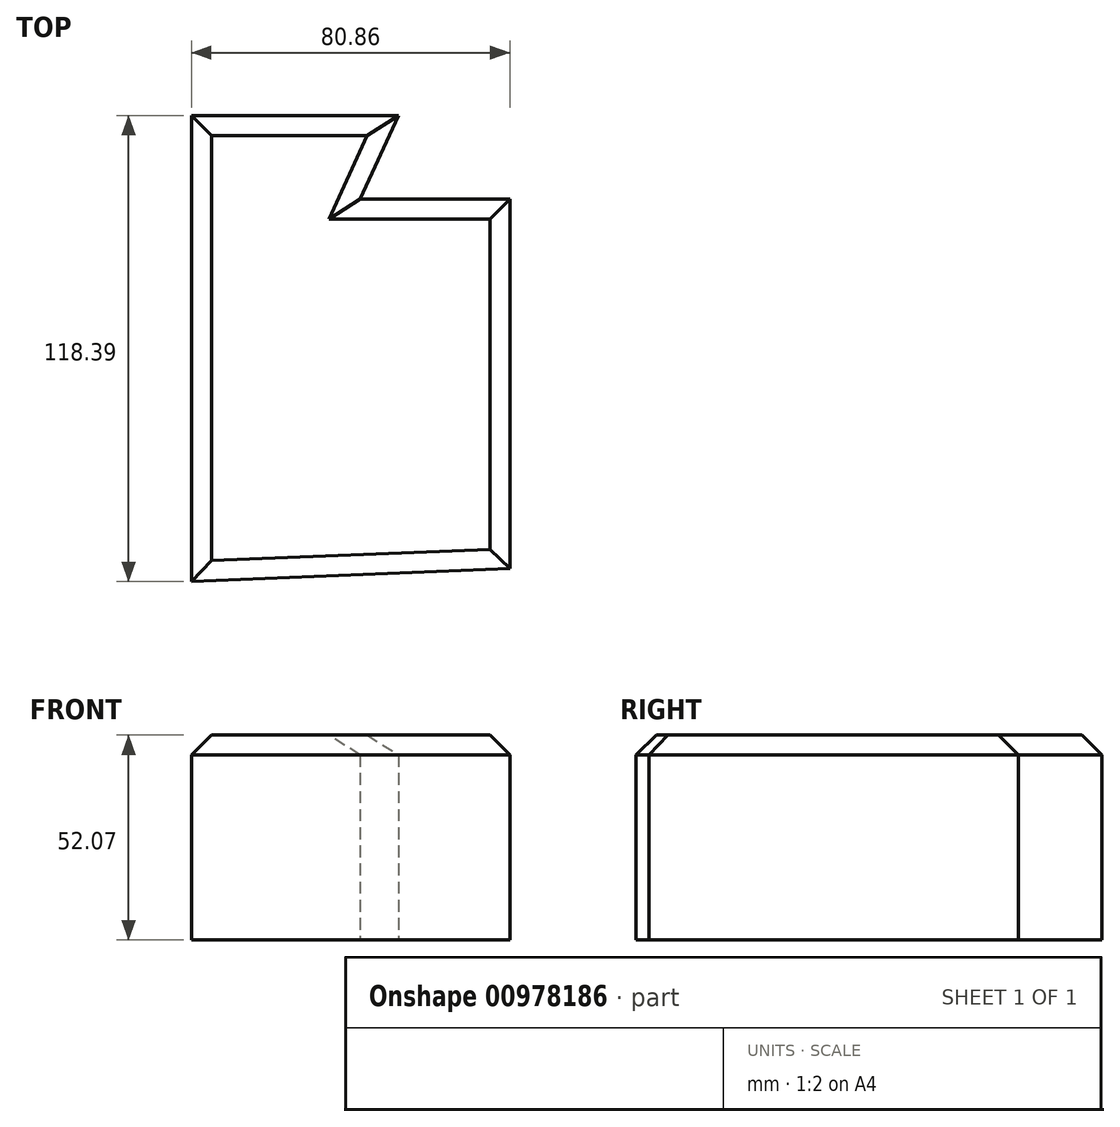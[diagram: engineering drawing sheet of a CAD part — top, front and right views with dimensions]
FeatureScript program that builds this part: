
annotation { "Feature Type Name" : "Feature", "Feature Type Description" : "" }
export const myFeature = defineFeature(function(context is Context, id is Id, definition is map)
    precondition{}
    {
        {
            var Q0;
            Q0=qCreatedBy(makeId("Top.planeOp"),FACE);
            var sketch = newSketch(context, id + "F0", { "sketchPlane" : qUnion([Q0])});
            skLineSegment(sketch, "E0", {"start": v(-64.11, -63.27) * mm, "end": v(-64.11, 55.12) * mm});
            skLineSegment(sketch, "E1", {"start": v(-64.11, 55.12) * mm, "end": v(-11.57, 55.12) * mm});
            skLineSegment(sketch, "E2", {"start": v(-11.57, 55.12) * mm, "end": v(-21.32, 33.95) * mm});
            skLineSegment(sketch, "E3", {"start": v(-21.32, 33.95) * mm, "end": v(16.75, 33.95) * mm});
            skLineSegment(sketch, "E4", {"start": v(16.75, 33.95) * mm, "end": v(16.75, -59.97) * mm});
            skLineSegment(sketch, "E5", {"start": v(16.75, -59.97) * mm, "end": v(-64.11, -63.27) * mm});
            skSolve(sketch);
        }
        {
            var Q0;
            Q0=makeQuery(id+"F0.imprint","IMPRINT",FACE,{"disambiguationData":[TD([[makeQuery(id+"F0.imprint","IMPRINT",EDGE,{"derivedFrom":sQuery(id+"F0.wireOp",EDGE,"E0")}),-1.0]])]});
            extrude(context, id + "F1", {"entities" : qUnion([Q0]), "depth" : 52.07 * mm, "offsetDistance" : 25.4 * mm});
        }
        {
            var Q0;
            Q0=makeQuery(id+"F1.opExtrude","CAP_EDGE",EDGE,{"disambiguationData":[OSD([sQuery(id+"F0.wireOp",EDGE,"E5")])],"isStart":false});
            var Q1;
            Q1=makeQuery(id+"F1.opExtrude","CAP_FACE",FACE,{"disambiguationData":[OSD([sQuery(id+"F0.wireOp",EDGE,"E0"),sQuery(id+"F0.wireOp",EDGE,"E1"),sQuery(id+"F0.wireOp",EDGE,"E2"),sQuery(id+"F0.wireOp",EDGE,"E3"),sQuery(id+"F0.wireOp",EDGE,"E4"),sQuery(id+"F0.wireOp",EDGE,"E5")])],"isStart":false});
            chamfer(context, id + "F2", {"entities" : qUnion([Q0, Q1]), "width" : 5.08 * mm, "tangentPropagation" : true});
        }
    });
